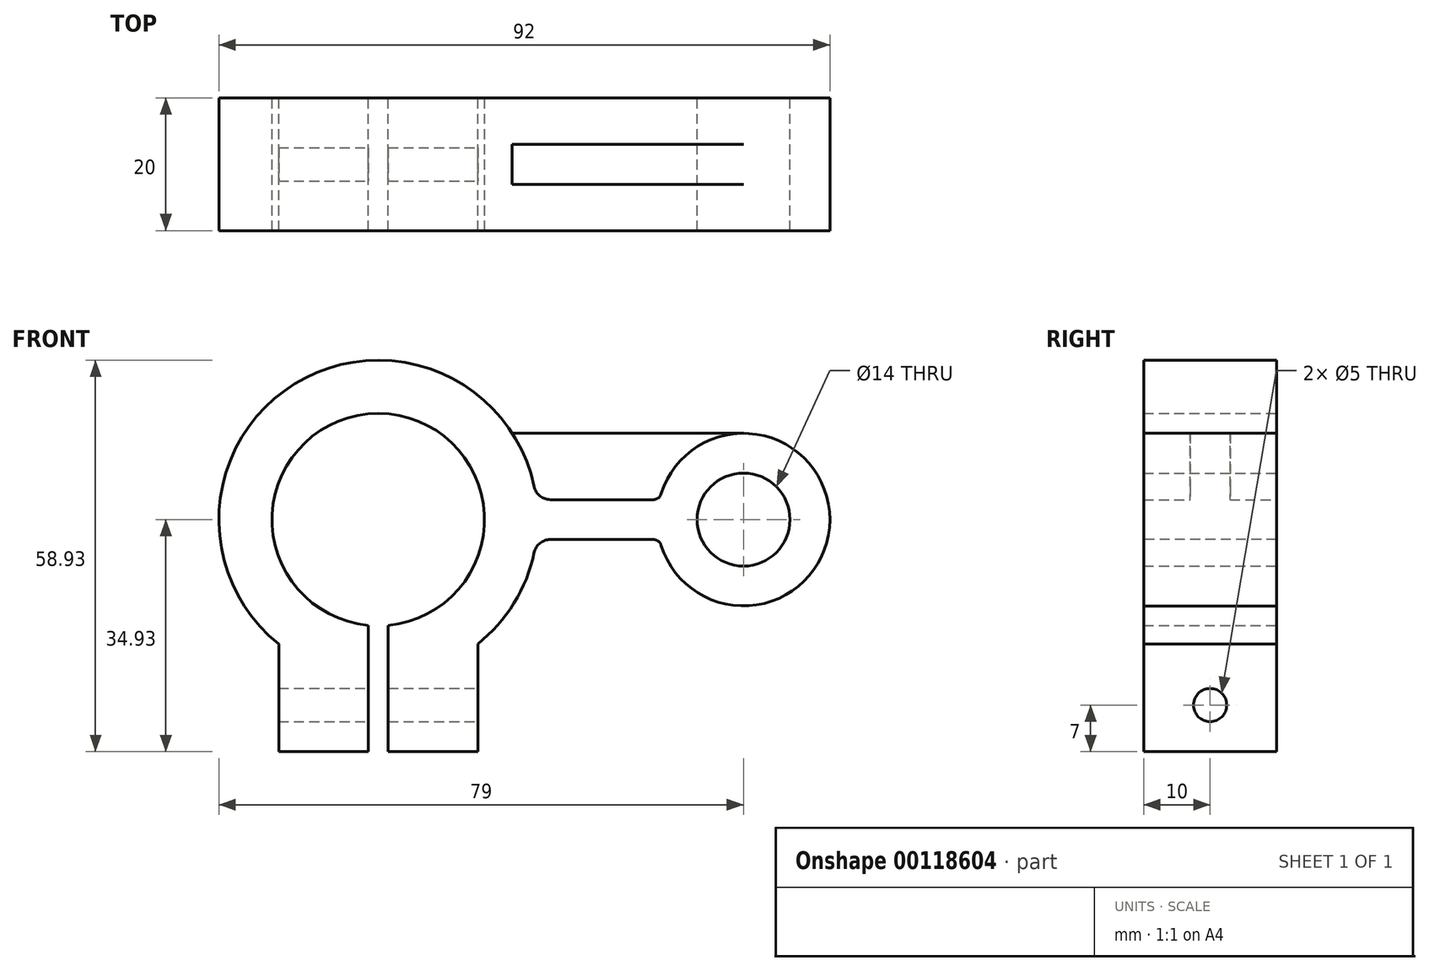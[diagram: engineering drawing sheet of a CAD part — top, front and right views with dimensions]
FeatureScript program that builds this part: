
annotation { "Feature Type Name" : "Feature", "Feature Type Description" : "" }
export const myFeature = defineFeature(function(context is Context, id is Id, definition is map)
    precondition{}
    {
        {
            var Q0;
            Q0=qCreatedBy(makeId("Front.planeOp"),FACE);
            var sketch = newSketch(context, id + "F0", { "sketchPlane" : qUnion([Q0])});
            skArc(sketch, "E0", {"start": v(1.5, -15.93) * mm, "mid": v(0, 16) * mm, "end": v(-1.5, -15.93) * mm});
            skArc(sketch, "E1", {"start": v(15, -18.73) * mm, "mid": v(20.94, -11.73) * mm, "end": v(23.81, -3) * mm});
            skCircle(sketch, "E2", {"center": v(55, 0) * mm, "radius": 7 * mm});
            skArc(sketch, "E3", {"start": v(42.35, -3) * mm, "mid": v(68, 0) * mm, "end": v(42.35, 3) * mm});
            skLineSegment(sketch, "E4.trimOffspring", {"start": v(23.81, 3) * mm, "end": v(42.35, 3) * mm});
            skLineSegment(sketch, "E5.trimOffspring", {"start": v(23.81, -3) * mm, "end": v(42.35, -3) * mm});
            skLineSegment(sketch, "E6.trimOffspring", {"start": v(15, -18.73) * mm, "end": v(15, -34.93) * mm});
            skLineSegment(sketch, "E7.trimOffspring", {"start": v(-15, -18.73) * mm, "end": v(-15, -34.93) * mm});
            skLineSegment(sketch, "E8.trimOffspring", {"start": v(1.5, -15.93) * mm, "end": v(1.5, -34.93) * mm});
            skLineSegment(sketch, "E9.trimOffspring", {"start": v(-1.5, -15.93) * mm, "end": v(-1.5, -34.93) * mm});
            skArc(sketch, "E10.trimOffspring", {"start": v(23.81, 3) * mm, "mid": v(-11.73, 20.94) * mm, "end": v(-15, -18.73) * mm});
            skLineSegment(sketch, "E11", {"start": v(-15, -34.93) * mm, "end": v(-1.5, -34.93) * mm});
            skLineSegment(sketch, "E12.trimOffspring", {"start": v(-1.5, -43.99) * mm, "end": v(-1.5, -44) * mm});
            skLineSegment(sketch, "E13.trimOffspring", {"start": v(1.5, -34.93) * mm, "end": v(15, -34.93) * mm});
            skLineSegment(sketch, "E14", {"start": v(55, 13) * mm, "end": v(20.17, 13) * mm});
            skSolve(sketch);
        }
        {
            var Q0;
            {var subQ0=sQuery(id+"F0.wireOp",EDGE,"E0");Q0=makeQuery(id+"F0.imprint","IMPRINT",FACE,{"disambiguationData":[TD([[makeQuery(id+"F0.imprint","IMPRINT",EDGE,{"derivedFrom":subQ0}),-1.0]])]});}
            extrude(context, id + "F1", {"entities" : qUnion([Q0]), "endBound" : BoundingType.SYMMETRIC, "depth" : 20 * mm});
        }
        {
            var Q0;
            Q0=makeQuery(id+"F1.opExtrude","SWEPT_FACE",FACE,{"disambiguationData":[OSD([sQuery(id+"F0.wireOp",EDGE,"E6.trimOffspring")])]});
            var sketch = newSketch(context, id + "F2", { "sketchPlane" : qUnion([Q0])});
            skCircle(sketch, "E15", {"center": v(0, -27.93) * mm, "radius": 2.5 * mm});
            skSolve(sketch);
        }
        {
            var Q0;
            Q0 = qSketchRegion(id + "F2", true);
            extrude(context, id + "F3", {"entities" : qUnion([Q0]), "operationType" : NewBodyOperationType.REMOVE, "endBound" : BoundingType.THROUGH_ALL, "oppositeDirection" : true, "depth" : 25 * mm});
        }
        {
            var Q0;
            Q0=makeQuery(id+"F1.opExtrude","SWEPT_EDGE",EDGE,{"disambiguationData":[OSD([sQuery(id+"F0.wireOp",EDGE,"E4.trimOffspring"),sQuery(id+"F0.wireOp",EDGE,"E10.trimOffspring")])]});
            var Q1;
            Q1=makeQuery(id+"F1.opExtrude","SWEPT_EDGE",EDGE,{"disambiguationData":[OSD([sQuery(id+"F0.wireOp",EDGE,"E1"),sQuery(id+"F0.wireOp",EDGE,"E5.trimOffspring")])]});
            fillet(context, id + "F4", {"entities" : qUnion([Q0, Q1]), "radius" : 2.5 * mm, "tangentPropagation" : true, "allowEdgeOverflow" : false});
        }
        {
            var Q0;
            Q0=makeQuery(id+"F1.opExtrude","SWEPT_EDGE",EDGE,{"disambiguationData":[OSD([sQuery(id+"F0.wireOp",EDGE,"E3"),sQuery(id+"F0.wireOp",EDGE,"E5.trimOffspring")])]});
            var Q1;
            Q1=makeQuery(id+"F1.opExtrude","SWEPT_EDGE",EDGE,{"disambiguationData":[OSD([sQuery(id+"F0.wireOp",EDGE,"E3"),sQuery(id+"F0.wireOp",EDGE,"E4.trimOffspring")])]});
            fillet(context, id + "F5", {"entities" : qUnion([Q0, Q1]), "radius" : 1.25 * mm, "tangentPropagation" : true, "allowEdgeOverflow" : false});
        }
        {
            var Q0;
            {var subQ0=sQuery(id+"F0.wireOp",EDGE,"E4.trimOffspring");Q0=makeQuery(id+"F0.imprint","IMPRINT",FACE,{"disambiguationData":[TD([[makeQuery(id+"F0.imprint","IMPRINT",EDGE,{"derivedFrom":subQ0}),1.0]])]});}
            extrude(context, id + "F6", {"entities" : qUnion([Q0]), "operationType" : NewBodyOperationType.ADD, "endBound" : BoundingType.SYMMETRIC, "depth" : 6 * mm});
        }
    });
